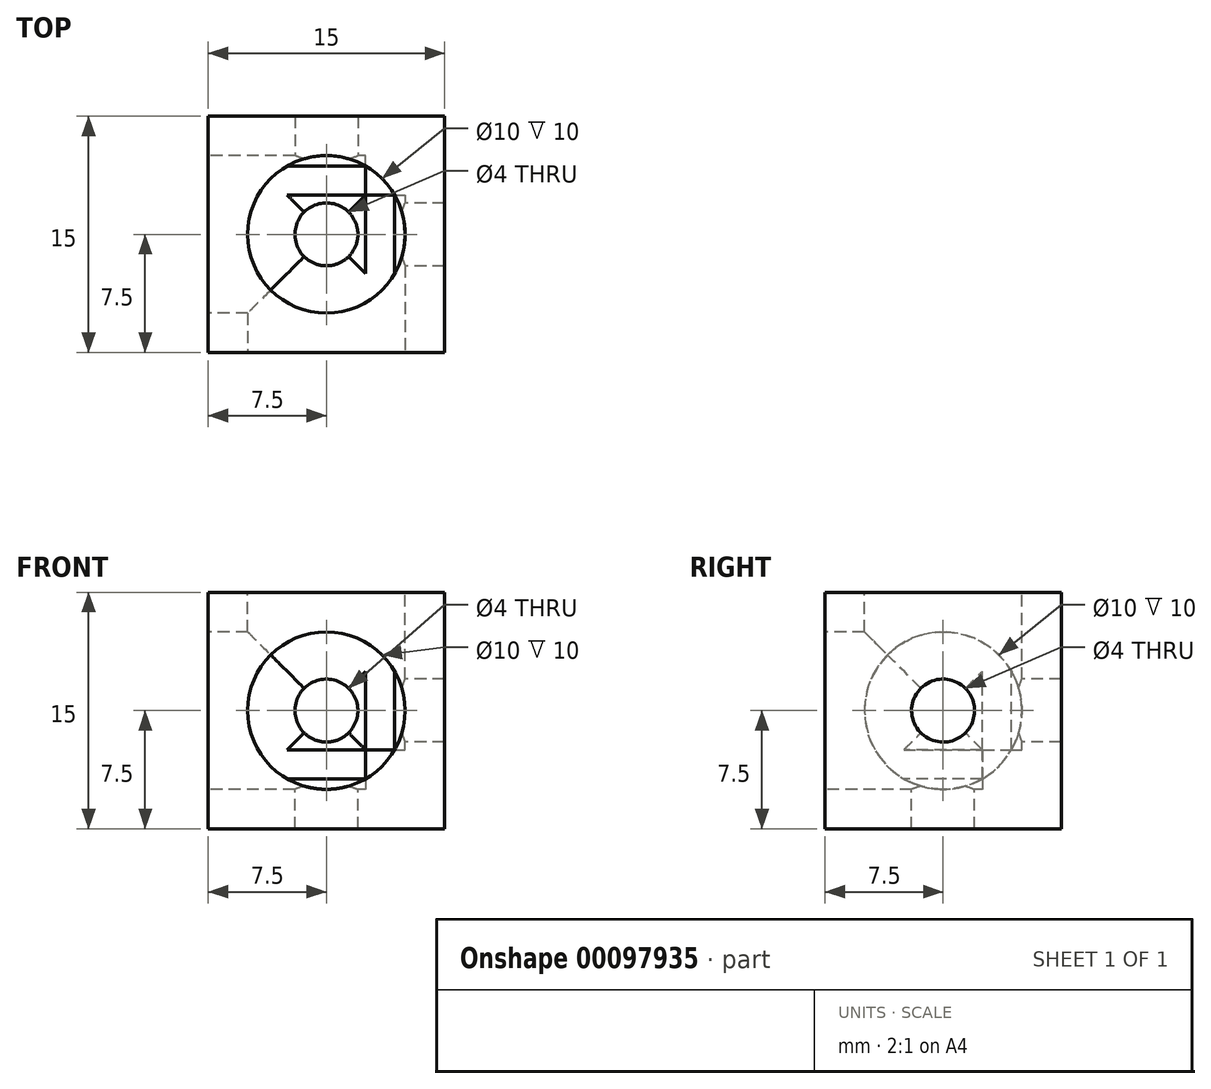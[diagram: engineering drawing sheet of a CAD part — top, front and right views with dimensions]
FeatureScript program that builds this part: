
annotation { "Feature Type Name" : "Feature", "Feature Type Description" : "" }
export const myFeature = defineFeature(function(context is Context, id is Id, definition is map)
    precondition{}
    {
        {
            var Q0;
            Q0=qCreatedBy(makeId("Front.planeOp"),FACE);
            var sketch = newSketch(context, id + "F0", { "sketchPlane" : qUnion([Q0])});
            skLineSegment(sketch, "E0.bottom", {"start": v(-7.5, 7.5) * mm, "end": v(7.5, 7.5) * mm});
            skLineSegment(sketch, "E0.top", {"start": v(-7.5, -7.5) * mm, "end": v(7.5, -7.5) * mm});
            skLineSegment(sketch, "E0.left", {"start": v(-7.5, 7.5) * mm, "end": v(-7.5, -7.5) * mm});
            skLineSegment(sketch, "E0.right", {"start": v(7.5, 7.5) * mm, "end": v(7.5, -7.5) * mm});
            skSolve(sketch);
        }
        {
            var Q0;
            Q0=makeQuery(id+"F0.imprint","IMPRINT",FACE,{"disambiguationData":[TD([[makeQuery(id+"F0.imprint","IMPRINT",EDGE,{"derivedFrom":sQuery(id+"F0.wireOp",EDGE,"E0.bottom")}),-1.0]])]});
            extrude(context, id + "F1", {"entities" : qUnion([Q0]), "endBound" : BoundingType.SYMMETRIC, "depth" : 15 * mm});
        }
        {
            var Q0;
            Q0=makeQuery(id+"F1.opExtrude","CAP_FACE",FACE,{"disambiguationData":[OSD([sQuery(id+"F0.wireOp",EDGE,"E0.bottom"),sQuery(id+"F0.wireOp",EDGE,"E0.top"),sQuery(id+"F0.wireOp",EDGE,"E0.left"),sQuery(id+"F0.wireOp",EDGE,"E0.right")])],"isStart":false});
            var sketch = newSketch(context, id + "F2", { "sketchPlane" : qUnion([Q0])});
            skPoint(sketch, "E1", {"position": v(0, 0) * mm});
            skSolve(sketch);
        }
        {
            var Q0;
            Q0=sQuery(id+"F2.wireOp",VERTEX,"E1");
            var Q1;
            Q1=makeQuery(id+"F1.opExtrude","SWEPT_BODY",BODY,{"disambiguationData":[OSD([sQuery(id+"F0.wireOp",EDGE,"E0.bottom"),sQuery(id+"F0.wireOp",EDGE,"E0.top"),sQuery(id+"F0.wireOp",EDGE,"E0.left"),sQuery(id+"F0.wireOp",EDGE,"E0.right")])]});
            hole(context, id + "F3", {"style" : HoleStyle.C_BORE, "endStyle" : HoleEndStyle.THROUGH, "holeDiameter" : 4 * mm, "cBoreDiameter" : 10 * mm, "cBoreDepth" : 10 * mm, "locations" : qUnion([Q0]), "scope" : qUnion([Q1]), "isTappedThrough" : true});
        }
        {
            var Q0;
            Q0=makeQuery(id+"F1.opExtrude","SWEPT_FACE",FACE,{"disambiguationData":[OSD([sQuery(id+"F0.wireOp",EDGE,"E0.left")])]});
            var sketch = newSketch(context, id + "F4", { "sketchPlane" : qUnion([Q0])});
            skPoint(sketch, "E2", {"position": v(0, 0) * mm});
            skSolve(sketch);
        }
        {
            var Q0;
            Q0=sQuery(id+"F4.wireOp",VERTEX,"E2");
            var Q1;
            Q1=makeQuery(id+"F1.opExtrude","SWEPT_BODY",BODY,{"disambiguationData":[OSD([sQuery(id+"F0.wireOp",EDGE,"E0.bottom"),sQuery(id+"F0.wireOp",EDGE,"E0.top"),sQuery(id+"F0.wireOp",EDGE,"E0.left"),sQuery(id+"F0.wireOp",EDGE,"E0.right")])]});
            hole(context, id + "F5", {"style" : HoleStyle.C_BORE, "endStyle" : HoleEndStyle.THROUGH, "holeDiameter" : 4 * mm, "cBoreDiameter" : 10 * mm, "cBoreDepth" : 10 * mm, "locations" : qUnion([Q0]), "scope" : qUnion([Q1]), "isTappedThrough" : true});
        }
        {
            var Q0;
            Q0=makeQuery(id+"F1.opExtrude","SWEPT_FACE",FACE,{"disambiguationData":[OSD([sQuery(id+"F0.wireOp",EDGE,"E0.bottom")])]});
            var sketch = newSketch(context, id + "F6", { "sketchPlane" : qUnion([Q0])});
            skPoint(sketch, "E3", {"position": v(0, 0) * mm});
            skSolve(sketch);
        }
        {
            var Q0;
            Q0=sQuery(id+"F6.wireOp",VERTEX,"E3");
            var Q1;
            Q1=makeQuery(id+"F1.opExtrude","SWEPT_BODY",BODY,{"disambiguationData":[OSD([sQuery(id+"F0.wireOp",EDGE,"E0.bottom"),sQuery(id+"F0.wireOp",EDGE,"E0.top"),sQuery(id+"F0.wireOp",EDGE,"E0.left"),sQuery(id+"F0.wireOp",EDGE,"E0.right")])]});
            hole(context, id + "F7", {"style" : HoleStyle.C_BORE, "endStyle" : HoleEndStyle.THROUGH, "holeDiameter" : 4 * mm, "cBoreDiameter" : 10 * mm, "cBoreDepth" : 10 * mm, "locations" : qUnion([Q0]), "scope" : qUnion([Q1]), "isTappedThrough" : true});
        }
    });
